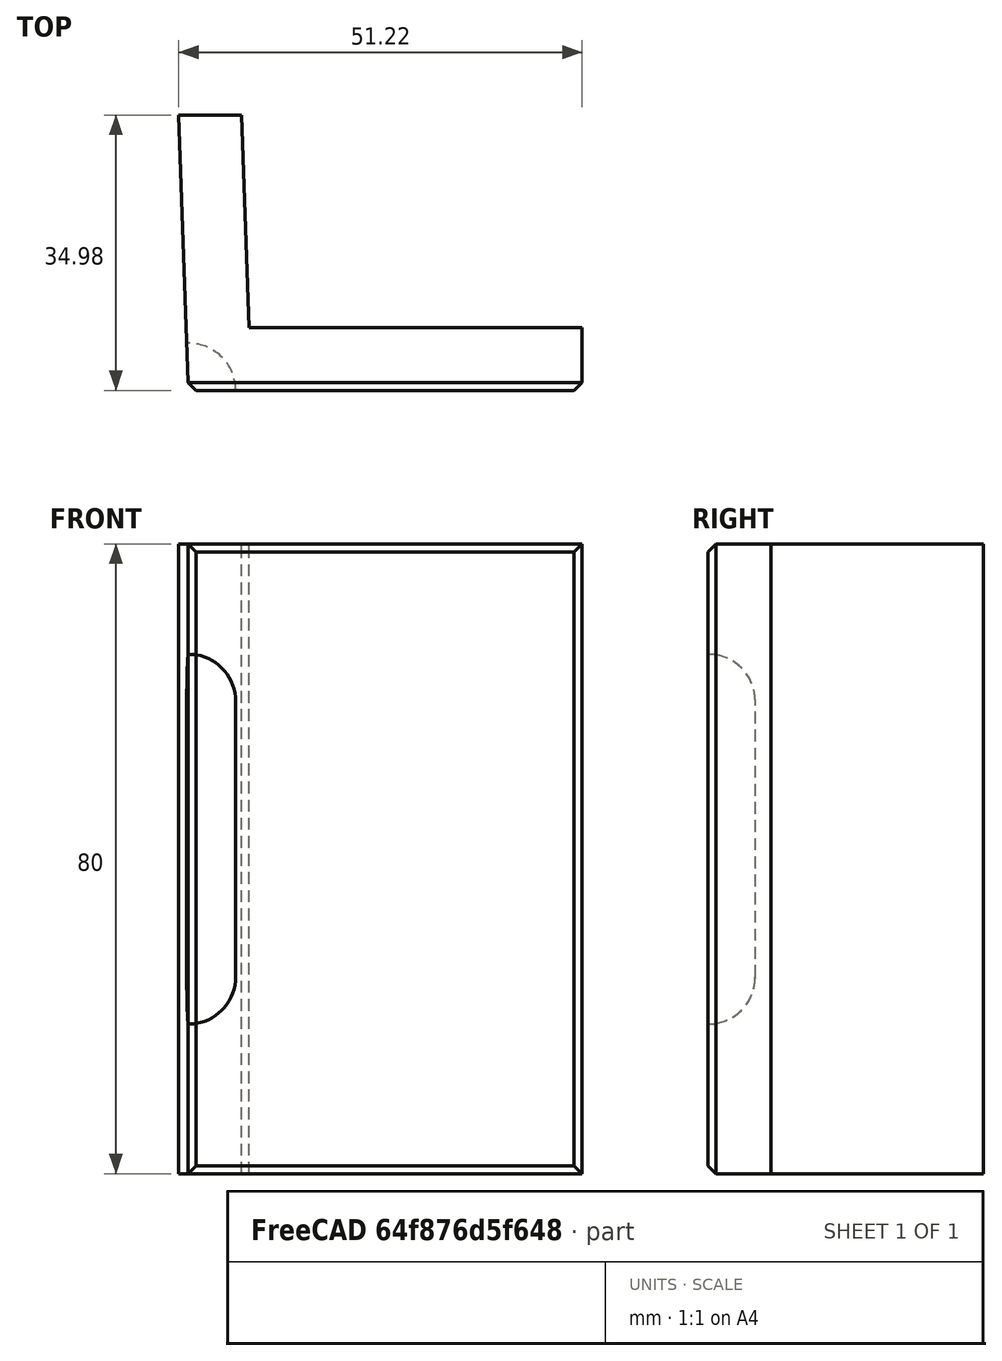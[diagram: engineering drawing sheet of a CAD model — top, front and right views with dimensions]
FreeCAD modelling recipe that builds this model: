
FCSTD DOCUMENT  (FreeCAD 0.19R)
Label: 88Edge
License: All rights reserved
LicenseURL: http://en.wikipedia.org/wiki/All_rights_reserved
objects: Sketcher::SketchObject×2, Part::Sphere×2, PartDesign::Pad×1, Part::Cylinder×1, PartDesign::Chamfer×1, PartDesign::Body×1, Part::MultiFuse×1, Part::Cut×1, Mesh::Feature×1
note: 12 computed .brp shape members not serialized (recipe doc carries the construction recipe); baked Part::Feature solids carry a one-line shape summary decoded from their .brp

FEATURE [Sketcher::SketchObject] Sketch
  FullyConstrained = true
  MapMode = 5
  Support = -> [XY_Plane]
  sketch-geometry (6):
    g0: LineSegment StartX=-1.22148 StartY=34.9787 StartZ=0 EndX=2e-16 EndY=0 EndZ=0
    g1: LineSegment StartX=0 StartY=0 StartZ=0 EndX=50 EndY=0 EndZ=0
    g2: LineSegment StartX=50 StartY=0 StartZ=0 EndX=50 EndY=8 EndZ=0
    g3: LineSegment StartX=50 StartY=8 StartZ=0 EndX=7.72063 EndY=8 EndZ=0
    g4: LineSegment StartX=7.72063 StartY=8 StartZ=0 EndX=6.77852 EndY=34.9787 EndZ=0
    g5: LineSegment StartX=6.77852 StartY=34.9787 StartZ=0 EndX=-1.22148 EndY=34.9787 EndZ=0
  constraints (17):
    c: Coincident(g0,g-1)
    c: Coincident(g0,g1)
    c: PointOnObject(g1,g-1)
    c: Coincident(g1,g2)
    c: Coincident(g2,g3)
    c: Horizontal(g3)
    c: Coincident(g3,g4)
    c: Coincident(g4,g5)
    c: Coincident(g5,g0)
    c: Horizontal(g5)
    c: Vertical(g2)
    c: Angle(g0) = -1.53589
    c: Parallel(g4,g0)
    c: Distance(g5) = 8
    c: Distance(g2) = 8
    c: Distance(g0) = 35
    c: Distance(g1) = 50
FEATURE [PartDesign::Pad] Pad
  Direction = (1,1,1)
  Length = 80
  Length2 = 100
  Profile = -> Sketch
  Type = 0
FEATURE [Sketcher::SketchObject] Sketch001
  ExternalGeometry = -> [Pad]
  FullyConstrained = true
  MapMode = 5
  Placement = pos=(7.99026,0.279026,0) rot=(0.563916,0.583952,0.583952;2.11466rad)
  Support = -> [Pad]
  sketch-geometry (4):
    g0: ArcOfCircle CenterX=12.7257 CenterY=55 CenterZ=0 NormalX=0 NormalY=0 NormalZ=1 AngleXU=0 Radius=5 StartAngle=0 EndAngle=3.14159
    g1: ArcOfCircle CenterX=12.7257 CenterY=25 CenterZ=0 NormalX=0 NormalY=0 NormalZ=1 AngleXU=0 Radius=5 StartAngle=3.14159 EndAngle=6.28319
    g2: LineSegment StartX=7.72568 StartY=55 StartZ=0 EndX=7.72568 EndY=25 EndZ=0
    g3: LineSegment StartX=17.7257 StartY=55 StartZ=0 EndX=17.7257 EndY=25 EndZ=0
  constraints (10):
    c: Tangent(g0,g3) = 1.5708
    c: Tangent(g0,g2) = -1.5708
    c: Tangent(g2,g1) = -1.5708
    c: Tangent(g3,g1) = 1.5708
    c: Vertical(g2)
    c: Equal(g0,g1)
    c: Distance(g0,g1) = 30
    c: Distance(g0,g0) = 10
    c: DistanceY(g1) = 25
    c: PointOnObject(g1,g-3)
FEATURE [Part::Cylinder] Cylinder
  Angle = 360
  AttacherType = Attacher::AttachEngine3D
  Height = 35
  Placement = pos=(0,0,25) rot=(0,0,1;0rad)
  Radius = 6
FEATURE [Part::Sphere] Sphere
  Angle1 = -90
  Angle2 = 90
  Angle3 = 360
  AttacherType = Attacher::AttachEngine3D
  Placement = pos=(0,0,25) rot=(0,0,1;0rad)
  Radius = 6
FEATURE [Part::Sphere] Sphere001
  Angle1 = -90
  Angle2 = 90
  Angle3 = 360
  AttacherType = Attacher::AttachEngine3D
  Placement = pos=(0,0,60) rot=(0,0,1;0rad)
  Radius = 6
FEATURE [PartDesign::Chamfer] Chamfer
  Angle = 45
  Base = -> Pad [Face2]
  BaseFeature = -> Pad
  ChamferType = 0
  FlipDirection = false
  Size = 1
  Size2 = 1
  SupportTransform = false
FEATURE [PartDesign::Body] Body
  Group = -> [Sketch,Pad,Sketch001,Chamfer]
  Origin = -> Origin
  Tip = -> Chamfer
FEATURE [Part::MultiFuse] Fusion
  Shapes = -> [Cylinder,Sphere,Sphere001]
FEATURE [Part::Cut] Cut
  Base = -> Chamfer
  Tool = -> Fusion
FEATURE [Mesh::Feature] Mesh  label="Cut (Meshed)"
